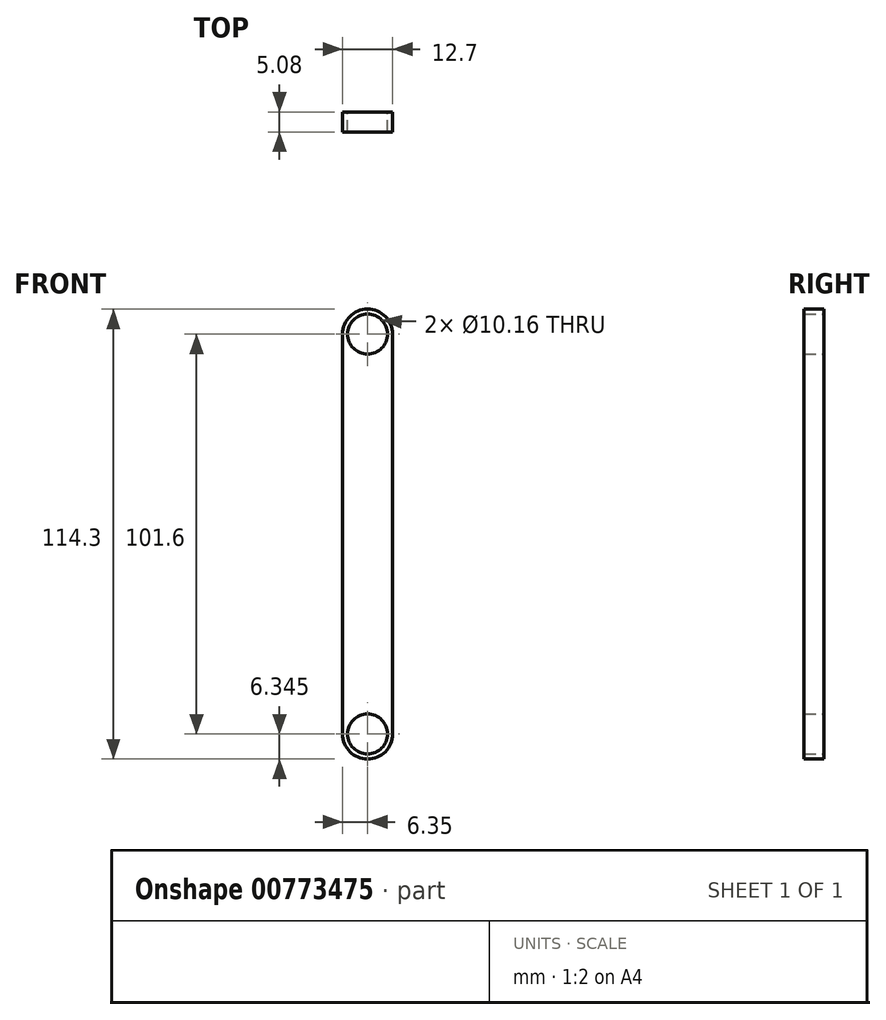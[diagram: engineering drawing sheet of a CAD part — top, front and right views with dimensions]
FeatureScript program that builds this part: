
annotation { "Feature Type Name" : "Feature", "Feature Type Description" : "" }
export const myFeature = defineFeature(function(context is Context, id is Id, definition is map)
    precondition{}
    {
        {
            var Q0;
            Q0=qCreatedBy(makeId("Front.planeOp"),FACE);
            var sketch = newSketch(context, id + "F0", { "sketchPlane" : qUnion([Q0])});
            skCircle(sketch, "E0", {"center": v(0, 80.36) * mm, "radius": 5.08 * mm});
            skCircle(sketch, "E1", {"center": v(0, 80.36) * mm, "radius": 6.35 * mm});
            skCircle(sketch, "E2", {"center": v(0, -21.24) * mm, "radius": 5.08 * mm});
            skCircle(sketch, "E3", {"center": v(0, -21.24) * mm, "radius": 6.35 * mm});
            skLineSegment(sketch, "E4", {"start": v(0, 80.36) * mm, "end": v(0, -21.24) * mm, "construction": true});
            skLineSegment(sketch, "E5", {"start": v(-6.35, 80.36) * mm, "end": v(-6.35, -21.24) * mm});
            skLineSegment(sketch, "E6", {"start": v(6.35, 80.36) * mm, "end": v(6.35, -21.24) * mm});
            skSolve(sketch);
        }
        {
            var Q0;
            {var subQ0=sQuery(id+"F0.wireOp",EDGE,"E5");Q0=makeQuery(id+"F0.imprint","IMPRINT",FACE,{"disambiguationData":[TD([[makeQuery(id+"F0.imprint","IMPRINT",EDGE,{"derivedFrom":subQ0}),1.0]])]});}
            var Q1;
            Q1=makeQuery(id+"F0.imprint","IMPRINT",FACE,{"disambiguationData":[TD([[makeQuery(id+"F0.imprint","IMPRINT",EDGE,{"derivedFrom":sQuery(id+"F0.wireOp",EDGE,"E0")}),-1.0]])]});
            var Q2;
            Q2=makeQuery(id+"F0.imprint","IMPRINT",FACE,{"disambiguationData":[TD([[makeQuery(id+"F0.imprint","IMPRINT",EDGE,{"derivedFrom":sQuery(id+"F0.wireOp",EDGE,"E2")}),-1.0]])]});
            extrude(context, id + "F1", {"entities" : qUnion([Q0, Q1, Q2]), "depth" : 5.08 * mm, "offsetDistance" : 25.4 * mm});
        }
    });
